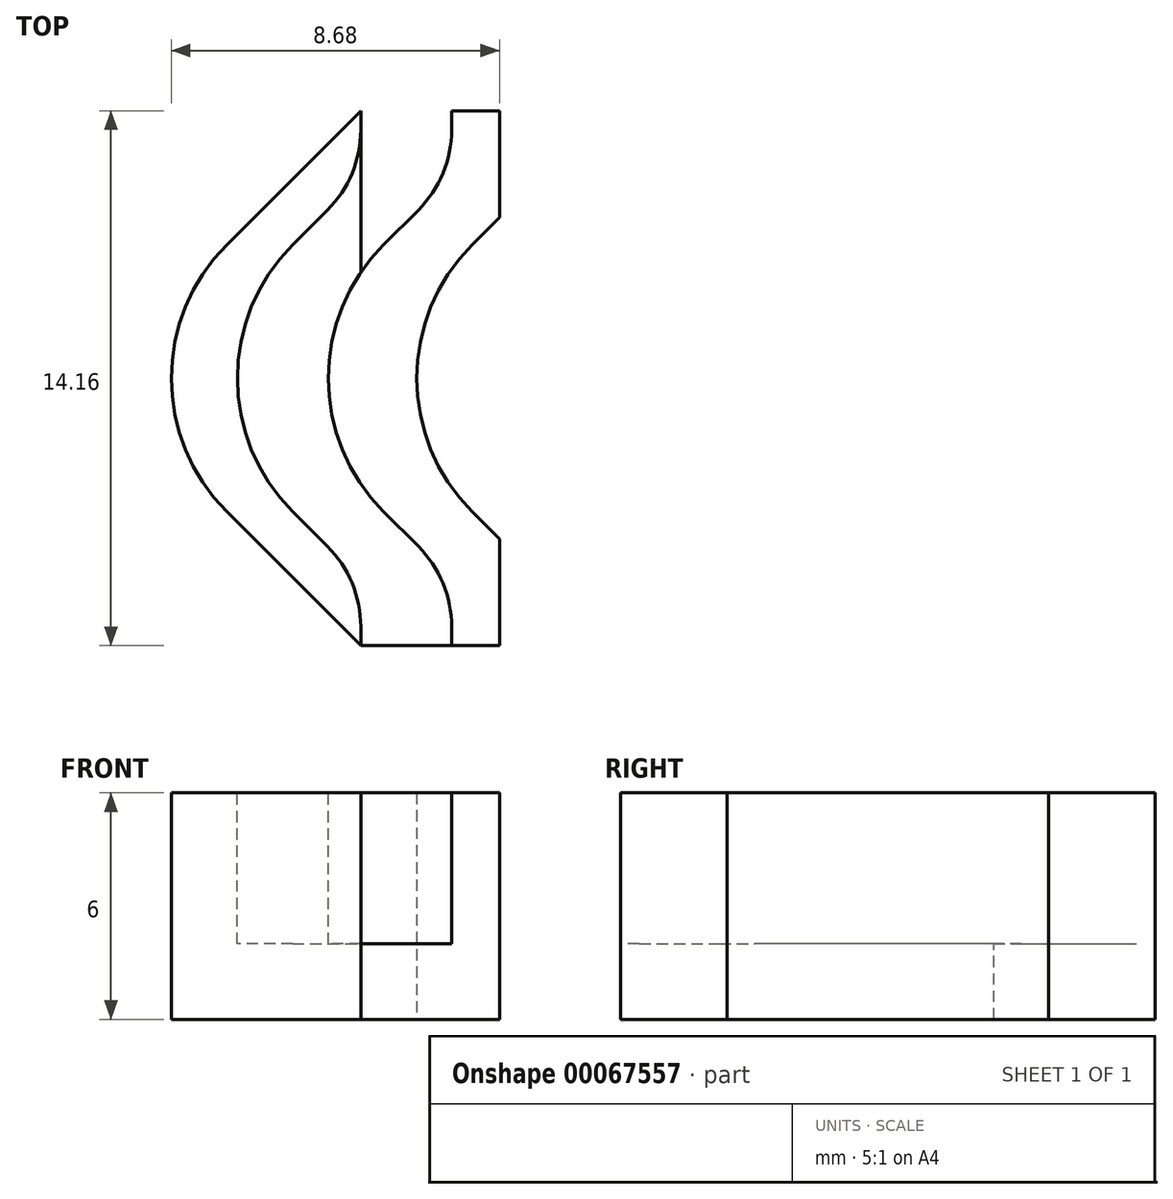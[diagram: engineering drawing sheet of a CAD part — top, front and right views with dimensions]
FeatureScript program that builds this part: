
annotation { "Feature Type Name" : "Feature", "Feature Type Description" : "" }
export const myFeature = defineFeature(function(context is Context, id is Id, definition is map)
    precondition{}
    {
        {
            var Q0;
            Q0=qCreatedBy(makeId("Top.planeOp"),FACE);
            var sketch = newSketch(context, id + "F0", { "sketchPlane" : qUnion([Q0])});
            skLineSegment(sketch, "E0", {"start": v(0, -9.89) * mm, "end": v(0, 9.57) * mm});
            skLineSegment(sketch, "E1", {"start": v(0, -5.33) * mm, "end": v(-5.33, 0) * mm});
            skLineSegment(sketch, "E2", {"start": v(-5.33, 0) * mm, "end": v(0, 5.33) * mm});
            skLineSegment(sketch, "E3.0", {"start": v(-2.93, 0) * mm, "end": v(2.4, 5.33) * mm});
            skLineSegment(sketch, "E3.1", {"start": v(2.4, -5.33) * mm, "end": v(-2.93, 0) * mm});
            skLineSegment(sketch, "E4", {"start": v(0, 5.33) * mm, "end": v(0, 7.08) * mm});
            skLineSegment(sketch, "E5", {"start": v(0, 7.08) * mm, "end": v(-7.08, 0) * mm});
            skLineSegment(sketch, "E6", {"start": v(-7.08, 0) * mm, "end": v(0, -7.08) * mm});
            skLineSegment(sketch, "E7", {"start": v(0, 7.08) * mm, "end": v(3.67, 7.08) * mm});
            skLineSegment(sketch, "E8", {"start": v(3.67, 7.08) * mm, "end": v(3.67, -7.08) * mm});
            skLineSegment(sketch, "E9", {"start": v(3.67, -7.08) * mm, "end": v(0, -7.08) * mm});
            skLineSegment(sketch, "E10", {"start": v(2.4, -5.33) * mm, "end": v(2.4, -7.08) * mm});
            skLineSegment(sketch, "E11", {"start": v(2.4, 5.33) * mm, "end": v(2.4, 7.08) * mm});
            skLineSegment(sketch, "E12", {"start": v(3.67, 4.26) * mm, "end": v(-0.59, 0) * mm});
            skLineSegment(sketch, "E13", {"start": v(-0.59, 0) * mm, "end": v(3.67, -4.26) * mm});
            skSolve(sketch);
        }
        {
            var Q0;
            {var subQ7=sQuery(id+"F0.wireOp",EDGE,"E11");Q0=makeQuery(id+"F0.imprint","IMPRINT",FACE,{"disambiguationData":[TD([[makeQuery(id+"F0.imprint","IMPRINT",EDGE,{"derivedFrom":subQ7}),-1.0]])]});}
            var Q1;
            {var subQ3=sQuery(id+"F0.wireOp",EDGE,"E10");Q1=makeQuery(id+"F0.imprint","IMPRINT",FACE,{"disambiguationData":[TD([[makeQuery(id+"F0.imprint","IMPRINT",EDGE,{"derivedFrom":subQ3}),1.0]])]});}
            var Q2;
            {var subQ3=sQuery(id+"F0.wireOp",EDGE,"E10");Q2=makeQuery(id+"F0.imprint","IMPRINT",FACE,{"disambiguationData":[TD([[makeQuery(id+"F0.imprint","IMPRINT",EDGE,{"derivedFrom":subQ3}),-1.0]])]});}
            var Q3;
            {var subQ1=sQuery(id+"F0.wireOp",EDGE,"E1");Q3=makeQuery(id+"F0.imprint","IMPRINT",FACE,{"disambiguationData":[TD([[makeQuery(id+"F0.imprint","IMPRINT",EDGE,{"derivedFrom":subQ1}),1.0]])]});}
            var Q4;
            {var subQ1=sQuery(id+"F0.wireOp",EDGE,"E4");Q4=makeQuery(id+"F0.imprint","IMPRINT",FACE,{"disambiguationData":[TD([[makeQuery(id+"F0.imprint","IMPRINT",EDGE,{"derivedFrom":subQ1}),-1.0]])]});}
            var Q5;
            {var subQ1=sQuery(id+"F0.wireOp",EDGE,"E1");Q5=makeQuery(id+"F0.imprint","IMPRINT",FACE,{"disambiguationData":[TD([[makeQuery(id+"F0.imprint","IMPRINT",EDGE,{"derivedFrom":subQ1}),-1.0]])]});}
            var Q6;
            {var subQ0=sQuery(id+"F0.wireOp",EDGE,"E3.1");var subQ3=sQuery(id+"F0.wireOp",EDGE,"E0");var subQ4=makeQuery(id+"F0.imprint","INTERSECT",VERTEX,{"derivedFrom":[subQ3,subQ0]});Q6=makeQuery(id+"F0.imprint","IMPRINT",FACE,{"disambiguationData":[TD([[makeQuery(id+"F0.imprint","IMPRINT",EDGE,{"disambiguationData":[TD([[subQ4,-1.0]])],"derivedFrom":subQ3}),1.0]])]});}
            extrude(context, id + "F1", {"entities" : qUnion([Q0, Q1, Q2, Q3, Q4, Q5, Q6]), "oppositeDirection" : true, "depth" : 2 * mm});
        }
        {
            var Q0;
            {var subQ1=sQuery(id+"F0.wireOp",EDGE,"E1");Q0=makeQuery(id+"F0.imprint","IMPRINT",FACE,{"disambiguationData":[TD([[makeQuery(id+"F0.imprint","IMPRINT",EDGE,{"derivedFrom":subQ1}),1.0]])]});}
            var Q1;
            {var subQ0=sQuery(id+"F0.wireOp",EDGE,"E3.1");var subQ3=sQuery(id+"F0.wireOp",EDGE,"E0");var subQ4=makeQuery(id+"F0.imprint","INTERSECT",VERTEX,{"derivedFrom":[subQ3,subQ0]});Q1=makeQuery(id+"F0.imprint","IMPRINT",FACE,{"disambiguationData":[TD([[makeQuery(id+"F0.imprint","IMPRINT",EDGE,{"disambiguationData":[TD([[subQ4,-1.0]])],"derivedFrom":subQ3}),1.0]])]});}
            var Q2;
            {var subQ7=sQuery(id+"F0.wireOp",EDGE,"E11");Q2=makeQuery(id+"F0.imprint","IMPRINT",FACE,{"disambiguationData":[TD([[makeQuery(id+"F0.imprint","IMPRINT",EDGE,{"derivedFrom":subQ7}),-1.0]])]});}
            var Q3;
            {var subQ3=sQuery(id+"F0.wireOp",EDGE,"E10");Q3=makeQuery(id+"F0.imprint","IMPRINT",FACE,{"disambiguationData":[TD([[makeQuery(id+"F0.imprint","IMPRINT",EDGE,{"derivedFrom":subQ3}),1.0]])]});}
            extrude(context, id + "F2", {"entities" : qUnion([Q0, Q1, Q2, Q3]), "operationType" : NewBodyOperationType.ADD, "depth" : 4 * mm});
        }
        {
            var Q0;
            Q0=makeQuery(id+"F2.opExtrude","SWEPT_EDGE",EDGE,{"disambiguationData":[OSD([sQuery(id+"F0.wireOp",EDGE,"E3.0"),sQuery(id+"F0.wireOp",EDGE,"E3.1")])]});
            var Q1;
            {var subQ0=sQuery(id+"F0.wireOp",EDGE,"E13");var subQ1=sQuery(id+"F0.wireOp",EDGE,"E12");Q1=makeQuery(id+"F2.boolean.opBoolean","MERGE",EDGE,{"derivedFrom":[makeQuery(id+"F1.opExtrude","SWEPT_EDGE",EDGE,{"disambiguationData":[OSD([subQ1,subQ0])]}),makeQuery(id+"F2.opExtrude","SWEPT_EDGE",EDGE,{"disambiguationData":[OSD([subQ1,subQ0])]})]});}
            var Q2;
            Q2=makeQuery(id+"F2.opExtrude","SWEPT_EDGE",EDGE,{"disambiguationData":[OSD([sQuery(id+"F0.wireOp",EDGE,"E1"),sQuery(id+"F0.wireOp",EDGE,"E2")])]});
            var Q3;
            {var subQ0=sQuery(id+"F0.wireOp",EDGE,"E6");var subQ1=sQuery(id+"F0.wireOp",EDGE,"E5");Q3=makeQuery(id+"F2.boolean.opBoolean","MERGE",EDGE,{"derivedFrom":[makeQuery(id+"F1.opExtrude","SWEPT_EDGE",EDGE,{"disambiguationData":[OSD([subQ1,subQ0])]}),makeQuery(id+"F2.opExtrude","SWEPT_EDGE",EDGE,{"disambiguationData":[OSD([subQ1,subQ0])]})]});}
            fillet(context, id + "F3", {"entities" : qUnion([Q0, Q1, Q2, Q3]), "radius" : 5 * mm, "tangentPropagation" : true, "allowEdgeOverflow" : false});
        }
        {
            var Q0;
            Q0=makeQuery(id+"F2.opExtrude","SWEPT_EDGE",EDGE,{"disambiguationData":[OSD([sQuery(id+"F0.wireOp",EDGE,"E3.1"),sQuery(id+"F0.wireOp",EDGE,"E10")])]});
            var Q1;
            Q1=makeQuery(id+"F2.opExtrude","SWEPT_EDGE",EDGE,{"disambiguationData":[OSD([sQuery(id+"F0.wireOp",EDGE,"E0"),sQuery(id+"F0.wireOp",EDGE,"E1")])]});
            var Q2;
            Q2=makeQuery(id+"F2.opExtrude","SWEPT_EDGE",EDGE,{"disambiguationData":[OSD([sQuery(id+"F0.wireOp",EDGE,"E0"),sQuery(id+"F0.wireOp",EDGE,"E2"),sQuery(id+"F0.wireOp",EDGE,"E4")])]});
            var Q3;
            Q3=makeQuery(id+"F2.opExtrude","SWEPT_EDGE",EDGE,{"disambiguationData":[OSD([sQuery(id+"F0.wireOp",EDGE,"E3.0"),sQuery(id+"F0.wireOp",EDGE,"E11")])]});
            fillet(context, id + "F4", {"entities" : qUnion([Q0, Q1, Q2, Q3]), "radius" : 3 * mm, "tangentPropagation" : true, "allowEdgeOverflow" : false});
        }
    });
